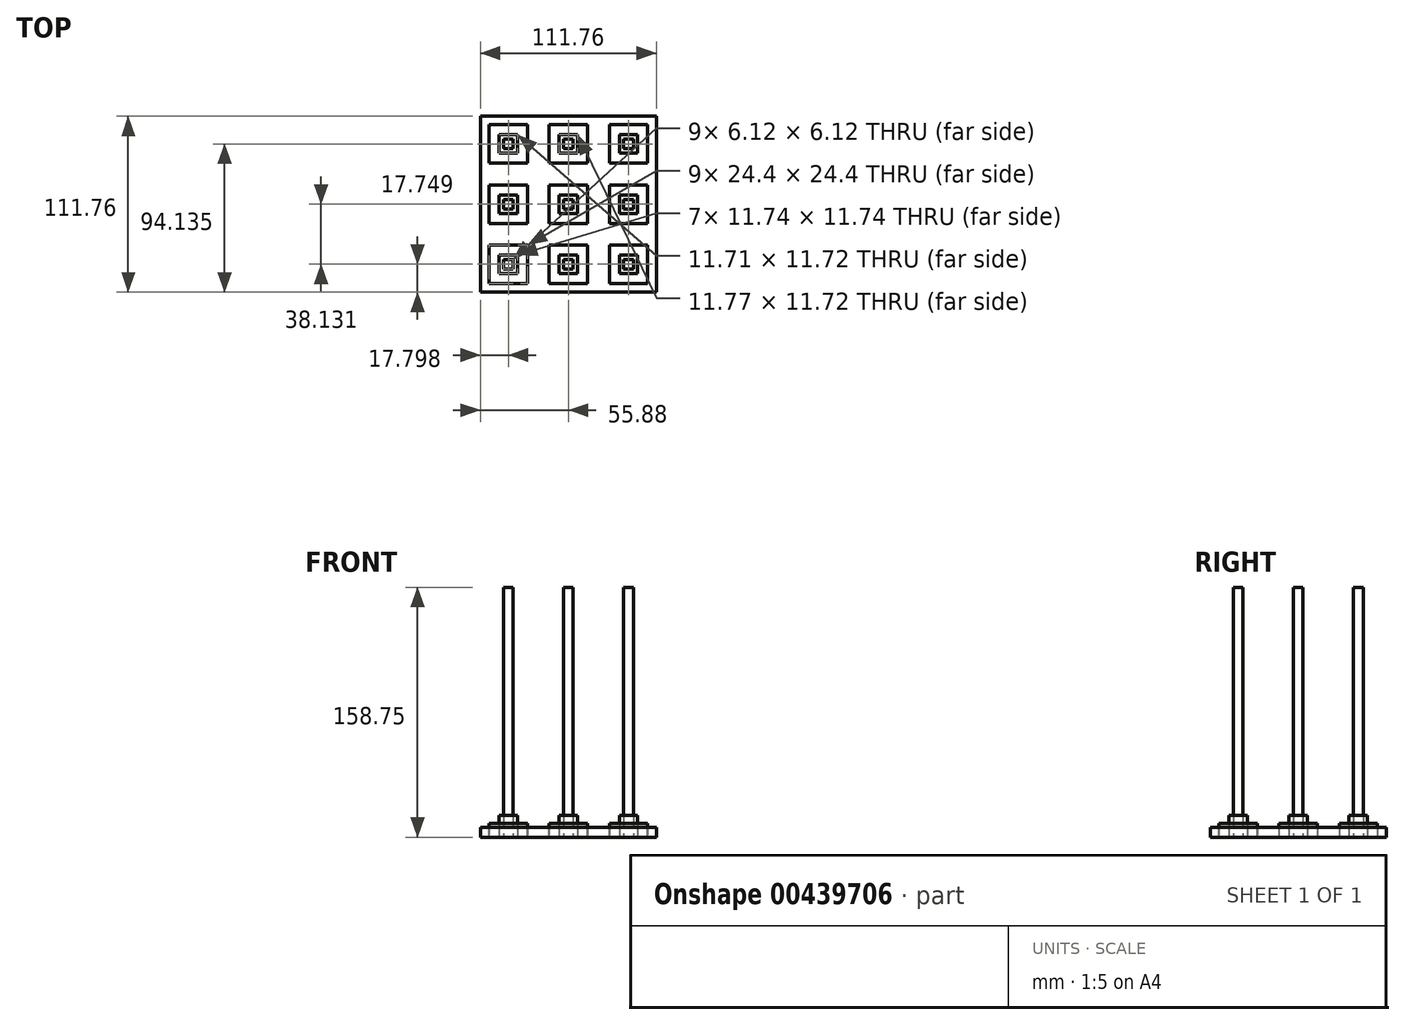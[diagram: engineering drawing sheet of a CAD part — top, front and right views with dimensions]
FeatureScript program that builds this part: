
annotation { "Feature Type Name" : "Feature", "Feature Type Description" : "" }
export const myFeature = defineFeature(function(context is Context, id is Id, definition is map)
    precondition{}
    {
        {
            var Q0;
            Q0=qCreatedBy(makeId("Top.planeOp"),FACE);
            var sketch = newSketch(context, id + "F0", { "sketchPlane" : qUnion([Q0])});
            skPoint(sketch, "E0", {"position": v(0, 38.25) * mm});
            skPoint(sketch, "E1", {"position": v(0, -38.13) * mm});
            skPoint(sketch, "E2", {"position": v(0, 0) * mm});
            skPoint(sketch, "E3", {"position": v(38.2, 38.25) * mm});
            skPoint(sketch, "E4", {"position": v(38.2, -38.13) * mm});
            skPoint(sketch, "E5", {"position": v(-38.08, -38.13) * mm});
            skPoint(sketch, "E6", {"position": v(-38.08, 38.25) * mm});
            skPoint(sketch, "E7", {"position": v(-38.08, 0) * mm});
            skPoint(sketch, "E8", {"position": v(38.2, 0) * mm});
            skLineSegment(sketch, "E9.bottom", {"start": v(-32.23, 32.4) * mm, "end": v(-43.94, 32.4) * mm});
            skLineSegment(sketch, "E9.top", {"start": v(-32.23, 44.12) * mm, "end": v(-43.94, 44.12) * mm});
            skLineSegment(sketch, "E9.left", {"start": v(-32.23, 32.4) * mm, "end": v(-32.23, 44.12) * mm});
            skLineSegment(sketch, "E9.right", {"start": v(-43.94, 32.4) * mm, "end": v(-43.94, 44.12) * mm});
            skLineSegment(sketch, "E10.bottom", {"start": v(5.88, 32.4) * mm, "end": v(-5.88, 32.4) * mm});
            skLineSegment(sketch, "E10.top", {"start": v(5.88, 44.12) * mm, "end": v(-5.88, 44.12) * mm});
            skLineSegment(sketch, "E10.left", {"start": v(5.88, 32.4) * mm, "end": v(5.88, 44.12) * mm});
            skLineSegment(sketch, "E10.right", {"start": v(-5.88, 32.4) * mm, "end": v(-5.88, 44.12) * mm});
            skLineSegment(sketch, "E11.bottom", {"start": v(44.07, 32.38) * mm, "end": v(32.33, 32.38) * mm});
            skLineSegment(sketch, "E11.top", {"start": v(44.07, 44.13) * mm, "end": v(32.33, 44.13) * mm});
            skLineSegment(sketch, "E11.left", {"start": v(44.07, 32.38) * mm, "end": v(44.07, 44.13) * mm});
            skLineSegment(sketch, "E11.right", {"start": v(32.33, 32.38) * mm, "end": v(32.33, 44.13) * mm});
            skLineSegment(sketch, "E12.bottom", {"start": v(-32.21, -5.87) * mm, "end": v(-43.95, -5.87) * mm});
            skLineSegment(sketch, "E12.top", {"start": v(-32.21, 5.87) * mm, "end": v(-43.95, 5.87) * mm});
            skLineSegment(sketch, "E12.left", {"start": v(-32.21, -5.87) * mm, "end": v(-32.21, 5.87) * mm});
            skLineSegment(sketch, "E12.right", {"start": v(-43.95, -5.87) * mm, "end": v(-43.95, 5.87) * mm});
            skLineSegment(sketch, "E13.bottom", {"start": v(5.87, -5.87) * mm, "end": v(-5.87, -5.87) * mm});
            skLineSegment(sketch, "E13.top", {"start": v(5.87, 5.87) * mm, "end": v(-5.87, 5.87) * mm});
            skLineSegment(sketch, "E13.left", {"start": v(5.87, -5.87) * mm, "end": v(5.87, 5.87) * mm});
            skLineSegment(sketch, "E13.right", {"start": v(-5.87, -5.87) * mm, "end": v(-5.87, 5.87) * mm});
            skLineSegment(sketch, "E14.bottom", {"start": v(44.07, -5.87) * mm, "end": v(32.33, -5.87) * mm});
            skLineSegment(sketch, "E14.top", {"start": v(44.07, 5.87) * mm, "end": v(32.33, 5.87) * mm});
            skLineSegment(sketch, "E14.left", {"start": v(44.07, -5.87) * mm, "end": v(44.07, 5.87) * mm});
            skLineSegment(sketch, "E14.right", {"start": v(32.33, -5.87) * mm, "end": v(32.33, 5.87) * mm});
            skLineSegment(sketch, "E15.bottom", {"start": v(32.33, -32.26) * mm, "end": v(44.07, -32.26) * mm});
            skLineSegment(sketch, "E15.top", {"start": v(32.33, -44) * mm, "end": v(44.07, -44) * mm});
            skLineSegment(sketch, "E15.left", {"start": v(32.33, -32.26) * mm, "end": v(32.33, -44) * mm});
            skLineSegment(sketch, "E15.right", {"start": v(44.07, -32.26) * mm, "end": v(44.07, -44) * mm});
            skLineSegment(sketch, "E16.bottom", {"start": v(5.87, -44) * mm, "end": v(-5.87, -44) * mm});
            skLineSegment(sketch, "E16.top", {"start": v(5.87, -32.26) * mm, "end": v(-5.87, -32.26) * mm});
            skLineSegment(sketch, "E16.left", {"start": v(5.87, -44) * mm, "end": v(5.87, -32.26) * mm});
            skLineSegment(sketch, "E16.right", {"start": v(-5.87, -44) * mm, "end": v(-5.87, -32.26) * mm});
            skLineSegment(sketch, "E17.bottom", {"start": v(-32.21, -44) * mm, "end": v(-43.95, -44) * mm});
            skLineSegment(sketch, "E17.top", {"start": v(-32.21, -32.26) * mm, "end": v(-43.95, -32.26) * mm});
            skLineSegment(sketch, "E17.left", {"start": v(-32.21, -44) * mm, "end": v(-32.21, -32.26) * mm});
            skLineSegment(sketch, "E17.right", {"start": v(-43.95, -44) * mm, "end": v(-43.95, -32.26) * mm});
            skLineSegment(sketch, "E18.bottom", {"start": v(-25.88, 26.05) * mm, "end": v(-50.28, 26.05) * mm});
            skLineSegment(sketch, "E18.top", {"start": v(-25.88, 50.46) * mm, "end": v(-50.28, 50.46) * mm});
            skLineSegment(sketch, "E18.left", {"start": v(-25.88, 26.05) * mm, "end": v(-25.88, 50.46) * mm});
            skLineSegment(sketch, "E18.right", {"start": v(-50.28, 26.05) * mm, "end": v(-50.28, 50.46) * mm});
            skLineSegment(sketch, "E19.bottom", {"start": v(12.2, 26.05) * mm, "end": v(-12.2, 26.05) * mm});
            skLineSegment(sketch, "E19.top", {"start": v(12.2, 50.46) * mm, "end": v(-12.2, 50.46) * mm});
            skLineSegment(sketch, "E19.left", {"start": v(12.2, 26.05) * mm, "end": v(12.2, 50.46) * mm});
            skLineSegment(sketch, "E19.right", {"start": v(-12.2, 26.05) * mm, "end": v(-12.2, 50.46) * mm});
            skLineSegment(sketch, "E20.bottom", {"start": v(50.4, 26.05) * mm, "end": v(26, 26.05) * mm});
            skLineSegment(sketch, "E20.top", {"start": v(50.4, 50.46) * mm, "end": v(26, 50.46) * mm});
            skLineSegment(sketch, "E20.left", {"start": v(50.4, 26.05) * mm, "end": v(50.4, 50.46) * mm});
            skLineSegment(sketch, "E20.right", {"start": v(26, 26.05) * mm, "end": v(26, 50.46) * mm});
            skLineSegment(sketch, "E21.bottom", {"start": v(-25.88, -12.2) * mm, "end": v(-50.28, -12.2) * mm});
            skLineSegment(sketch, "E21.top", {"start": v(-25.88, 12.2) * mm, "end": v(-50.28, 12.2) * mm});
            skLineSegment(sketch, "E21.left", {"start": v(-25.88, -12.2) * mm, "end": v(-25.88, 12.2) * mm});
            skLineSegment(sketch, "E21.right", {"start": v(-50.28, -12.2) * mm, "end": v(-50.28, 12.2) * mm});
            skLineSegment(sketch, "E22.bottom", {"start": v(12.2, -12.2) * mm, "end": v(-12.2, -12.2) * mm});
            skLineSegment(sketch, "E22.top", {"start": v(12.2, 12.2) * mm, "end": v(-12.2, 12.2) * mm});
            skLineSegment(sketch, "E22.left", {"start": v(12.2, -12.2) * mm, "end": v(12.2, 12.2) * mm});
            skLineSegment(sketch, "E22.right", {"start": v(-12.2, -12.2) * mm, "end": v(-12.2, 12.2) * mm});
            skLineSegment(sketch, "E23.bottom", {"start": v(50.4, -12.2) * mm, "end": v(26, -12.2) * mm});
            skLineSegment(sketch, "E23.top", {"start": v(50.4, 12.2) * mm, "end": v(26, 12.2) * mm});
            skLineSegment(sketch, "E23.left", {"start": v(50.4, -12.2) * mm, "end": v(50.4, 12.2) * mm});
            skLineSegment(sketch, "E23.right", {"start": v(26, -12.2) * mm, "end": v(26, 12.2) * mm});
            skLineSegment(sketch, "E24.bottom", {"start": v(50.4, -50.33) * mm, "end": v(26, -50.33) * mm});
            skLineSegment(sketch, "E24.top", {"start": v(50.4, -25.93) * mm, "end": v(26, -25.93) * mm});
            skLineSegment(sketch, "E24.left", {"start": v(50.4, -50.33) * mm, "end": v(50.4, -25.93) * mm});
            skLineSegment(sketch, "E24.right", {"start": v(26, -50.33) * mm, "end": v(26, -25.93) * mm});
            skLineSegment(sketch, "E25.bottom", {"start": v(12.2, -50.33) * mm, "end": v(-12.2, -50.33) * mm});
            skLineSegment(sketch, "E25.top", {"start": v(12.2, -25.93) * mm, "end": v(-12.2, -25.93) * mm});
            skLineSegment(sketch, "E25.left", {"start": v(12.2, -50.33) * mm, "end": v(12.2, -25.93) * mm});
            skLineSegment(sketch, "E25.right", {"start": v(-12.2, -50.33) * mm, "end": v(-12.2, -25.93) * mm});
            skLineSegment(sketch, "E26.bottom", {"start": v(-25.88, -50.33) * mm, "end": v(-50.28, -50.33) * mm});
            skLineSegment(sketch, "E26.top", {"start": v(-25.88, -25.93) * mm, "end": v(-50.28, -25.93) * mm});
            skLineSegment(sketch, "E26.left", {"start": v(-25.88, -50.33) * mm, "end": v(-25.88, -25.93) * mm});
            skLineSegment(sketch, "E26.right", {"start": v(-50.28, -50.33) * mm, "end": v(-50.28, -25.93) * mm});
            skLineSegment(sketch, "E27.bottom", {"start": v(55.88, -55.88) * mm, "end": v(-55.88, -55.88) * mm});
            skLineSegment(sketch, "E27.top", {"start": v(55.88, 55.88) * mm, "end": v(-55.88, 55.88) * mm});
            skLineSegment(sketch, "E27.left", {"start": v(55.88, -55.88) * mm, "end": v(55.88, 55.88) * mm});
            skLineSegment(sketch, "E27.right", {"start": v(-55.88, -55.88) * mm, "end": v(-55.88, 55.88) * mm});
            skLineSegment(sketch, "E28.bottom", {"start": v(-35.02, 35.2) * mm, "end": v(-41.14, 35.2) * mm});
            skLineSegment(sketch, "E28.top", {"start": v(-35.02, 41.32) * mm, "end": v(-41.14, 41.32) * mm});
            skLineSegment(sketch, "E28.left", {"start": v(-35.02, 35.2) * mm, "end": v(-35.02, 41.32) * mm});
            skLineSegment(sketch, "E28.right", {"start": v(-41.14, 35.2) * mm, "end": v(-41.14, 41.32) * mm});
            skLineSegment(sketch, "E29.bottom", {"start": v(3.06, 35.2) * mm, "end": v(-3.06, 35.2) * mm});
            skLineSegment(sketch, "E29.top", {"start": v(3.06, 41.32) * mm, "end": v(-3.06, 41.32) * mm});
            skLineSegment(sketch, "E29.left", {"start": v(3.06, 35.2) * mm, "end": v(3.06, 41.32) * mm});
            skLineSegment(sketch, "E29.right", {"start": v(-3.06, 35.2) * mm, "end": v(-3.06, 41.32) * mm});
            skLineSegment(sketch, "E30.bottom", {"start": v(41.26, 35.2) * mm, "end": v(35.14, 35.2) * mm});
            skLineSegment(sketch, "E30.top", {"start": v(41.26, 41.32) * mm, "end": v(35.14, 41.32) * mm});
            skLineSegment(sketch, "E30.left", {"start": v(41.26, 35.2) * mm, "end": v(41.26, 41.32) * mm});
            skLineSegment(sketch, "E30.right", {"start": v(35.14, 35.2) * mm, "end": v(35.14, 41.32) * mm});
            skLineSegment(sketch, "E31.bottom", {"start": v(-35.02, -3.06) * mm, "end": v(-41.14, -3.06) * mm});
            skLineSegment(sketch, "E31.top", {"start": v(-35.02, 3.06) * mm, "end": v(-41.14, 3.06) * mm});
            skLineSegment(sketch, "E31.left", {"start": v(-35.02, -3.06) * mm, "end": v(-35.02, 3.06) * mm});
            skLineSegment(sketch, "E31.right", {"start": v(-41.14, -3.06) * mm, "end": v(-41.14, 3.06) * mm});
            skLineSegment(sketch, "E32.bottom", {"start": v(3.06, -3.06) * mm, "end": v(-3.06, -3.06) * mm});
            skLineSegment(sketch, "E32.top", {"start": v(3.06, 3.06) * mm, "end": v(-3.06, 3.06) * mm});
            skLineSegment(sketch, "E32.left", {"start": v(3.06, -3.06) * mm, "end": v(3.06, 3.06) * mm});
            skLineSegment(sketch, "E32.right", {"start": v(-3.06, -3.06) * mm, "end": v(-3.06, 3.06) * mm});
            skLineSegment(sketch, "E33.bottom", {"start": v(41.26, -3.06) * mm, "end": v(35.14, -3.06) * mm});
            skLineSegment(sketch, "E33.top", {"start": v(41.26, 3.06) * mm, "end": v(35.14, 3.06) * mm});
            skLineSegment(sketch, "E33.left", {"start": v(41.26, -3.06) * mm, "end": v(41.26, 3.06) * mm});
            skLineSegment(sketch, "E33.right", {"start": v(35.14, -3.06) * mm, "end": v(35.14, 3.06) * mm});
            skLineSegment(sketch, "E34.bottom", {"start": v(3.06, -41.2) * mm, "end": v(-3.06, -41.2) * mm});
            skLineSegment(sketch, "E34.top", {"start": v(3.06, -35.07) * mm, "end": v(-3.06, -35.07) * mm});
            skLineSegment(sketch, "E34.left", {"start": v(3.06, -41.2) * mm, "end": v(3.06, -35.07) * mm});
            skLineSegment(sketch, "E34.right", {"start": v(-3.06, -41.2) * mm, "end": v(-3.06, -35.07) * mm});
            skLineSegment(sketch, "E35.bottom", {"start": v(41.26, -41.2) * mm, "end": v(35.14, -41.2) * mm});
            skLineSegment(sketch, "E35.top", {"start": v(41.26, -35.07) * mm, "end": v(35.14, -35.07) * mm});
            skLineSegment(sketch, "E35.left", {"start": v(41.26, -41.2) * mm, "end": v(41.26, -35.07) * mm});
            skLineSegment(sketch, "E35.right", {"start": v(35.14, -41.2) * mm, "end": v(35.14, -35.07) * mm});
            skLineSegment(sketch, "E36.bottom", {"start": v(-35.02, -41.2) * mm, "end": v(-41.14, -41.2) * mm});
            skLineSegment(sketch, "E36.top", {"start": v(-35.02, -35.07) * mm, "end": v(-41.14, -35.07) * mm});
            skLineSegment(sketch, "E36.left", {"start": v(-35.02, -41.2) * mm, "end": v(-35.02, -35.07) * mm});
            skLineSegment(sketch, "E36.right", {"start": v(-41.14, -41.2) * mm, "end": v(-41.14, -35.07) * mm});
            skSolve(sketch);
        }
        {
            var Q0;
            Q0=makeQuery(id+"F0.imprint","IMPRINT",FACE,{"disambiguationData":[TD([[makeQuery(id+"F0.imprint","IMPRINT",EDGE,{"derivedFrom":sQuery(id+"F0.wireOp",EDGE,"E12.bottom")}),1.0]])]});
            var Q1;
            Q1=makeQuery(id+"F0.imprint","IMPRINT",FACE,{"disambiguationData":[TD([[makeQuery(id+"F0.imprint","IMPRINT",EDGE,{"derivedFrom":sQuery(id+"F0.wireOp",EDGE,"E9.bottom")}),1.0]])]});
            var Q2;
            Q2=makeQuery(id+"F0.imprint","IMPRINT",FACE,{"disambiguationData":[TD([[makeQuery(id+"F0.imprint","IMPRINT",EDGE,{"derivedFrom":sQuery(id+"F0.wireOp",EDGE,"E10.bottom")}),1.0]])]});
            var Q3;
            Q3=makeQuery(id+"F0.imprint","IMPRINT",FACE,{"disambiguationData":[TD([[makeQuery(id+"F0.imprint","IMPRINT",EDGE,{"derivedFrom":sQuery(id+"F0.wireOp",EDGE,"E11.bottom")}),1.0]])]});
            var Q4;
            Q4=makeQuery(id+"F0.imprint","IMPRINT",FACE,{"disambiguationData":[TD([[makeQuery(id+"F0.imprint","IMPRINT",EDGE,{"derivedFrom":sQuery(id+"F0.wireOp",EDGE,"E14.bottom")}),1.0]])]});
            var Q5;
            Q5=makeQuery(id+"F0.imprint","IMPRINT",FACE,{"disambiguationData":[TD([[makeQuery(id+"F0.imprint","IMPRINT",EDGE,{"derivedFrom":sQuery(id+"F0.wireOp",EDGE,"E15.bottom")}),1.0]])]});
            var Q6;
            Q6=makeQuery(id+"F0.imprint","IMPRINT",FACE,{"disambiguationData":[TD([[makeQuery(id+"F0.imprint","IMPRINT",EDGE,{"derivedFrom":sQuery(id+"F0.wireOp",EDGE,"E16.bottom")}),1.0]])]});
            var Q7;
            Q7=makeQuery(id+"F0.imprint","IMPRINT",FACE,{"disambiguationData":[TD([[makeQuery(id+"F0.imprint","IMPRINT",EDGE,{"derivedFrom":sQuery(id+"F0.wireOp",EDGE,"E17.bottom")}),1.0]])]});
            var Q8;
            Q8=makeQuery(id+"F0.imprint","IMPRINT",FACE,{"disambiguationData":[TD([[makeQuery(id+"F0.imprint","IMPRINT",EDGE,{"derivedFrom":sQuery(id+"F0.wireOp",EDGE,"E13.bottom")}),1.0]])]});
            extrude(context, id + "F1", {"entities" : qUnion([Q0, Q1, Q2, Q3, Q4, Q5, Q6, Q7, Q8]), "depth" : 2.54 * mm, "hasSecondDirection" : true, "secondDirectionOppositeDirection" : true, "secondDirectionDepth" : 6.35 * mm});
        }
        {
            var Q0;
            Q0=makeQuery(id+"F0.imprint","IMPRINT",FACE,{"disambiguationData":[TD([[makeQuery(id+"F0.imprint","IMPRINT",EDGE,{"derivedFrom":sQuery(id+"F0.wireOp",EDGE,"E18.bottom")}),1.0]])]});
            extrude(context, id + "F2", {"entities" : qUnion([Q0]), "oppositeDirection" : true, "depth" : 6.35 * mm});
        }
        {
            var Q0;
            Q0=makeQuery(id+"F0.imprint","IMPRINT",FACE,{"disambiguationData":[TD([[makeQuery(id+"F0.imprint","IMPRINT",EDGE,{"derivedFrom":sQuery(id+"F0.wireOp",EDGE,"E9.bottom")}),-1.0]])]});
            var Q1;
            Q1=makeQuery(id+"F0.imprint","IMPRINT",FACE,{"disambiguationData":[TD([[makeQuery(id+"F0.imprint","IMPRINT",EDGE,{"derivedFrom":sQuery(id+"F0.wireOp",EDGE,"E10.bottom")}),-1.0]])]});
            var Q2;
            Q2=makeQuery(id+"F0.imprint","IMPRINT",FACE,{"disambiguationData":[TD([[makeQuery(id+"F0.imprint","IMPRINT",EDGE,{"derivedFrom":sQuery(id+"F0.wireOp",EDGE,"E11.bottom")}),-1.0]])]});
            var Q3;
            Q3=makeQuery(id+"F0.imprint","IMPRINT",FACE,{"disambiguationData":[TD([[makeQuery(id+"F0.imprint","IMPRINT",EDGE,{"derivedFrom":sQuery(id+"F0.wireOp",EDGE,"E14.bottom")}),-1.0]])]});
            var Q4;
            Q4=makeQuery(id+"F0.imprint","IMPRINT",FACE,{"disambiguationData":[TD([[makeQuery(id+"F0.imprint","IMPRINT",EDGE,{"derivedFrom":sQuery(id+"F0.wireOp",EDGE,"E13.bottom")}),-1.0]])]});
            var Q5;
            Q5=makeQuery(id+"F0.imprint","IMPRINT",FACE,{"disambiguationData":[TD([[makeQuery(id+"F0.imprint","IMPRINT",EDGE,{"derivedFrom":sQuery(id+"F0.wireOp",EDGE,"E12.bottom")}),-1.0]])]});
            var Q6;
            Q6=makeQuery(id+"F0.imprint","IMPRINT",FACE,{"disambiguationData":[TD([[makeQuery(id+"F0.imprint","IMPRINT",EDGE,{"derivedFrom":sQuery(id+"F0.wireOp",EDGE,"E17.bottom")}),-1.0]])]});
            var Q7;
            Q7=makeQuery(id+"F0.imprint","IMPRINT",FACE,{"disambiguationData":[TD([[makeQuery(id+"F0.imprint","IMPRINT",EDGE,{"derivedFrom":sQuery(id+"F0.wireOp",EDGE,"E16.bottom")}),-1.0]])]});
            var Q8;
            Q8=makeQuery(id+"F0.imprint","IMPRINT",FACE,{"disambiguationData":[TD([[makeQuery(id+"F0.imprint","IMPRINT",EDGE,{"derivedFrom":sQuery(id+"F0.wireOp",EDGE,"E15.bottom")}),-1.0]])]});
            extrude(context, id + "F3", {"entities" : qUnion([Q0, Q1, Q2, Q3, Q4, Q5, Q6, Q7, Q8]), "depth" : 7.62 * mm, "hasSecondDirection" : true, "secondDirectionOppositeDirection" : true, "secondDirectionDepth" : 6.35 * mm});
        }
        {
            var Q0;
            Q0=makeQuery(id+"F0.imprint","IMPRINT",FACE,{"disambiguationData":[TD([[makeQuery(id+"F0.imprint","IMPRINT",EDGE,{"derivedFrom":sQuery(id+"F0.wireOp",EDGE,"E31.bottom")}),-1.0]])]});
            var Q1;
            Q1=makeQuery(id+"F0.imprint","IMPRINT",FACE,{"disambiguationData":[TD([[makeQuery(id+"F0.imprint","IMPRINT",EDGE,{"derivedFrom":sQuery(id+"F0.wireOp",EDGE,"E28.bottom")}),-1.0]])]});
            var Q2;
            Q2=makeQuery(id+"F0.imprint","IMPRINT",FACE,{"disambiguationData":[TD([[makeQuery(id+"F0.imprint","IMPRINT",EDGE,{"derivedFrom":sQuery(id+"F0.wireOp",EDGE,"E29.bottom")}),-1.0]])]});
            var Q3;
            Q3=makeQuery(id+"F0.imprint","IMPRINT",FACE,{"disambiguationData":[TD([[makeQuery(id+"F0.imprint","IMPRINT",EDGE,{"derivedFrom":sQuery(id+"F0.wireOp",EDGE,"E30.bottom")}),-1.0]])]});
            var Q4;
            Q4=makeQuery(id+"F0.imprint","IMPRINT",FACE,{"disambiguationData":[TD([[makeQuery(id+"F0.imprint","IMPRINT",EDGE,{"derivedFrom":sQuery(id+"F0.wireOp",EDGE,"E33.bottom")}),-1.0]])]});
            var Q5;
            Q5=makeQuery(id+"F0.imprint","IMPRINT",FACE,{"disambiguationData":[TD([[makeQuery(id+"F0.imprint","IMPRINT",EDGE,{"derivedFrom":sQuery(id+"F0.wireOp",EDGE,"E32.bottom")}),-1.0]])]});
            var Q6;
            Q6=makeQuery(id+"F0.imprint","IMPRINT",FACE,{"disambiguationData":[TD([[makeQuery(id+"F0.imprint","IMPRINT",EDGE,{"derivedFrom":sQuery(id+"F0.wireOp",EDGE,"E34.bottom")}),-1.0]])]});
            var Q7;
            Q7=makeQuery(id+"F0.imprint","IMPRINT",FACE,{"disambiguationData":[TD([[makeQuery(id+"F0.imprint","IMPRINT",EDGE,{"derivedFrom":sQuery(id+"F0.wireOp",EDGE,"E35.bottom")}),-1.0]])]});
            var Q8;
            Q8=makeQuery(id+"F0.imprint","IMPRINT",FACE,{"disambiguationData":[TD([[makeQuery(id+"F0.imprint","IMPRINT",EDGE,{"derivedFrom":sQuery(id+"F0.wireOp",EDGE,"E36.bottom")}),-1.0]])]});
            extrude(context, id + "F4", {"entities" : qUnion([Q0, Q1, Q2, Q3, Q4, Q5, Q6, Q7, Q8]), "depth" : 152.4 * mm, "hasSecondDirection" : true, "secondDirectionOppositeDirection" : true, "secondDirectionDepth" : 6.35 * mm});
        }
    });
